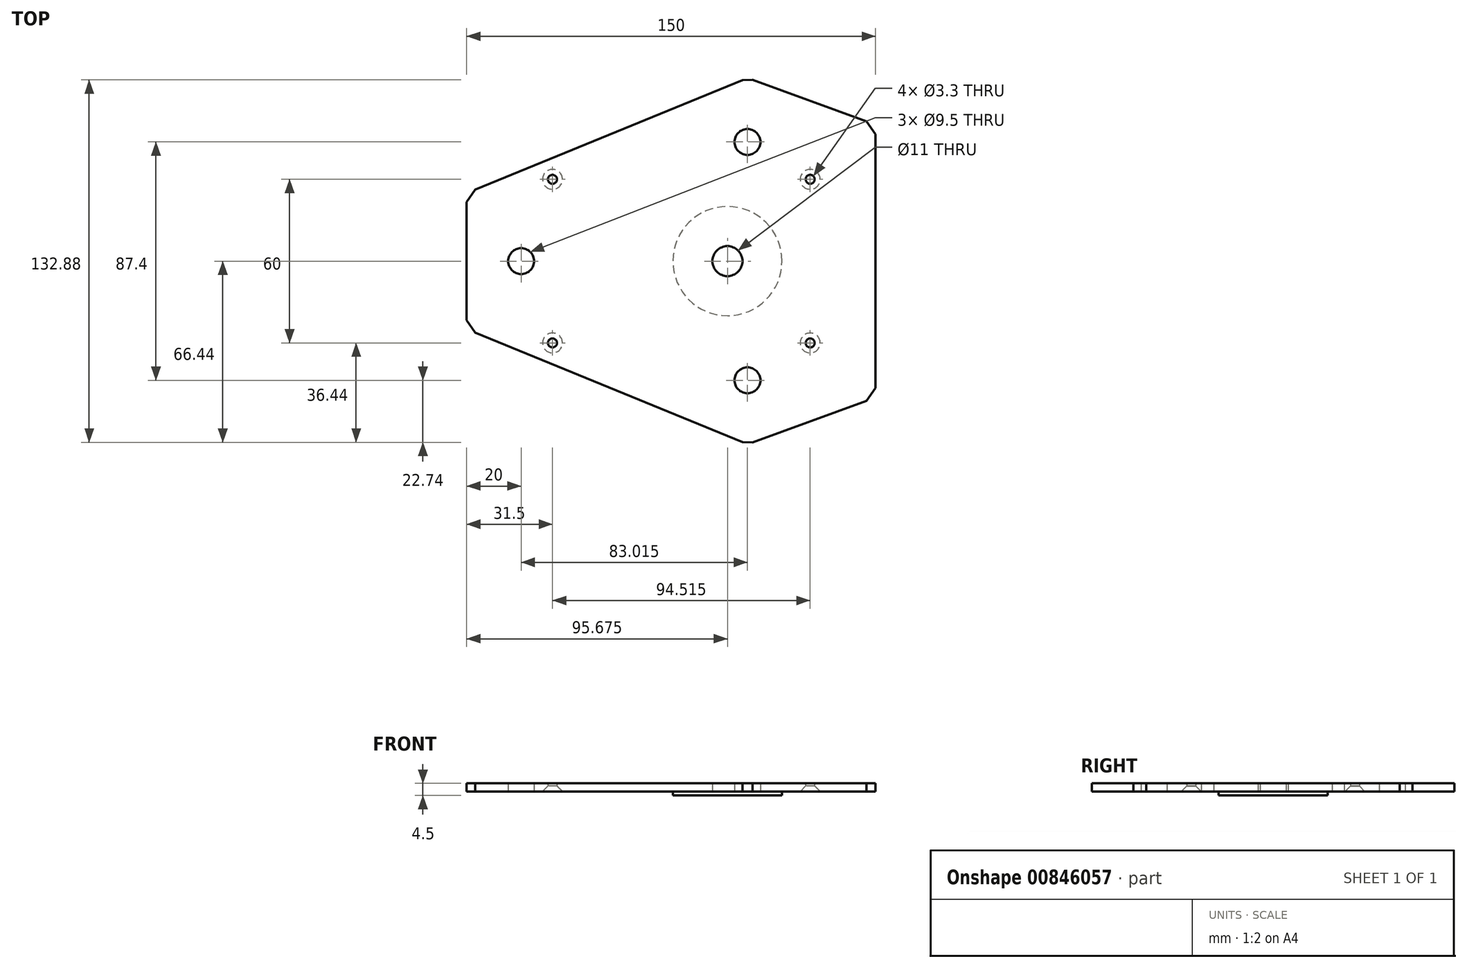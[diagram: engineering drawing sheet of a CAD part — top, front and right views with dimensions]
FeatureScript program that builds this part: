
annotation { "Feature Type Name" : "Feature", "Feature Type Description" : "" }
export const myFeature = defineFeature(function(context is Context, id is Id, definition is map)
    precondition{}
    {
        {
            var Q0;
            Q0=qCreatedBy(makeId("Top.planeOp"),FACE);
            var sketch = newSketch(context, id + "F0", { "sketchPlane" : qUnion([Q0])});
            skLineSegment(sketch, "E0", {"start": v(74.5, 0) * mm, "end": v(74.5, -50) * mm});
            skLineSegment(sketch, "E1", {"start": v(74.5, 0) * mm, "end": v(74.5, 50) * mm});
            skLineSegment(sketch, "E2", {"start": v(74.5, 50) * mm, "end": v(27.52, 67.1) * mm});
            skLineSegment(sketch, "E3", {"start": v(-75.5, 0) * mm, "end": v(-75.5, 25) * mm});
            skLineSegment(sketch, "E4", {"start": v(-75.5, 0) * mm, "end": v(-75.5, -25) * mm});
            skLineSegment(sketch, "E5", {"start": v(-75.5, 25) * mm, "end": v(27.52, 67.1) * mm});
            skLineSegment(sketch, "E6", {"start": v(-75.5, 0) * mm, "end": v(74.5, 0) * mm});
            skLineSegment(sketch, "E7.MirrorCS", {"start": v(74.5, -50) * mm, "end": v(27.52, -67.1) * mm});
            skLineSegment(sketch, "E8", {"start": v(-75.5, -25) * mm, "end": v(27.52, -67.1) * mm});
            skLineSegment(sketch, "E9.bottom", {"start": v(-32.18, 14.6) * mm, "end": v(-21.68, 14.6) * mm});
            skLineSegment(sketch, "E9.top", {"start": v(-32.18, -14.6) * mm, "end": v(-21.68, -14.6) * mm});
            skLineSegment(sketch, "E9.right", {"start": v(31.17, 14.6) * mm, "end": v(31.17, 1.3) * mm});
            skLineSegment(sketch, "E10", {"start": v(-21.68, 14.6) * mm, "end": v(-21.68, 16.53) * mm});
            skLineSegment(sketch, "E11", {"start": v(-13.48, 14.6) * mm, "end": v(-13.48, 16.53) * mm});
            skArc(sketch, "E12", {"start": v(-13.48, 16.53) * mm, "mid": v(-17.58, 20.63) * mm, "end": v(-21.68, 16.53) * mm});
            skLineSegment(sketch, "E13.trimOffspring", {"start": v(-13.48, 14.6) * mm, "end": v(12.48, 14.6) * mm});
            skArc(sketch, "E14.MirrorCS", {"start": v(12.48, 16.53) * mm, "mid": v(16.58, 20.63) * mm, "end": v(20.68, 16.53) * mm});
            skLineSegment(sketch, "E15.MirrorCS", {"start": v(20.68, 14.6) * mm, "end": v(20.68, 16.53) * mm});
            skLineSegment(sketch, "E16.MirrorCS", {"start": v(12.48, 14.6) * mm, "end": v(12.48, 16.53) * mm});
            skLineSegment(sketch, "E17.MirrorCS", {"start": v(-21.68, -14.6) * mm, "end": v(-21.68, -16.53) * mm});
            skArc(sketch, "E18.MirrorCS", {"start": v(-13.48, -16.53) * mm, "mid": v(-17.58, -20.63) * mm, "end": v(-21.68, -16.53) * mm});
            skLineSegment(sketch, "E19.MirrorCS", {"start": v(-13.48, -14.6) * mm, "end": v(-13.48, -16.53) * mm});
            skLineSegment(sketch, "E20.MirrorCS", {"start": v(12.47, -14.6) * mm, "end": v(12.48, -16.53) * mm});
            skArc(sketch, "E21.MirrorCS", {"start": v(12.47, -16.53) * mm, "mid": v(16.57, -20.63) * mm, "end": v(20.67, -16.53) * mm});
            skLineSegment(sketch, "E22.MirrorCS", {"start": v(20.67, -14.6) * mm, "end": v(20.67, -16.53) * mm});
            skLineSegment(sketch, "E23.trimOffspring", {"start": v(-13.48, -14.6) * mm, "end": v(12.47, -14.6) * mm});
            skLineSegment(sketch, "E24.trimOffspring", {"start": v(20.67, -14.6) * mm, "end": v(31.17, -14.6) * mm});
            skLineSegment(sketch, "E25.trimOffspring", {"start": v(20.68, 14.6) * mm, "end": v(31.17, 14.6) * mm});
            skPoint(sketch, "E26.end.orphan", {"position": v(31.17, 0) * mm});
            skPoint(sketch, "E26.start.orphan", {"position": v(-32.18, 0) * mm});
            skLineSegment(sketch, "E27.trimOffspring", {"start": v(-32.18, -1.3) * mm, "end": v(-32.18, -14.6) * mm});
            skLineSegment(sketch, "E28", {"start": v(-32.18, 1.3) * mm, "end": v(-32.18, 14.6) * mm});
            skLineSegment(sketch, "E29.MirrorCS", {"start": v(31.17, 1.3) * mm, "end": v(38.76, 1.3) * mm});
            skLineSegment(sketch, "E30.MirrorCS", {"start": v(38.76, 1.3) * mm, "end": v(38.76, -1.3) * mm});
            skLineSegment(sketch, "E31.MirrorCS", {"start": v(31.17, -1.3) * mm, "end": v(38.76, -1.3) * mm});
            skLineSegment(sketch, "E32", {"start": v(-32.17, 1.3) * mm, "end": v(-32.17, -1.3) * mm});
            skLineSegment(sketch, "E33.trimOffspring", {"start": v(31.17, -1.3) * mm, "end": v(31.17, -14.6) * mm});
            skCircle(sketch, "E34", {"center": v(-55.5, 0) * mm, "radius": 4.75 * mm});
            skCircle(sketch, "E35", {"center": v(-44, 30) * mm, "radius": 1.65 * mm});
            skCircle(sketch, "E36.MirrorC", {"center": v(-44, -30) * mm, "radius": 1.65 * mm});
            skCircle(sketch, "E37", {"center": v(27.52, 43.7) * mm, "radius": 4.75 * mm});
            skCircle(sketch, "E38.MirrorC", {"center": v(27.52, -43.7) * mm, "radius": 4.75 * mm});
            skCircle(sketch, "E39", {"center": v(50.52, 30) * mm, "radius": 1.65 * mm});
            skCircle(sketch, "E40.MirrorC", {"center": v(50.52, -30) * mm, "radius": 1.65 * mm});
            skCircle(sketch, "E41", {"center": v(20.18, 0) * mm, "radius": 5.5 * mm});
            skSolve(sketch);
        }
        {
            var Q0;
            {var subQ8=sQuery(id+"F0.wireOp",EDGE,"E1");Q0=makeQuery(id+"F0.imprint","IMPRINT",FACE,{"disambiguationData":[TD([[makeQuery(id+"F0.imprint","IMPRINT",EDGE,{"derivedFrom":subQ8}),1.0]])]});}
            var Q1;
            {var subQ11=sQuery(id+"F0.wireOp",EDGE,"E0");Q1=makeQuery(id+"F0.imprint","IMPRINT",FACE,{"disambiguationData":[TD([[makeQuery(id+"F0.imprint","IMPRINT",EDGE,{"derivedFrom":subQ11}),-1.0]])]});}
            var Q2;
            Q2=makeQuery(id+"F0.imprint","IMPRINT",FACE,{"disambiguationData":[TD([[makeQuery(id+"F0.imprint","IMPRINT",EDGE,{"derivedFrom":sQuery(id+"F0.wireOp",EDGE,"E9.top")}),1.0]])]});
            var Q3;
            Q3=makeQuery(id+"F0.imprint","IMPRINT",FACE,{"disambiguationData":[TD([[makeQuery(id+"F0.imprint","IMPRINT",EDGE,{"derivedFrom":sQuery(id+"F0.wireOp",EDGE,"E9.bottom")}),-1.0]])]});
            extrude(context, id + "F1", {"entities" : qUnion([Q0, Q1, Q2, Q3]), "depth" : 3 * mm, "offsetDistance" : 25 * mm});
        }
        {
            var Q0;
            Q0=makeQuery(id+"F1.opExtrude","CAP_EDGE",EDGE,{"disambiguationData":[OSD([sQuery(id+"F0.wireOp",EDGE,"E36.MirrorC")])],"isStart":true});
            var Q1;
            Q1=makeQuery(id+"F1.opExtrude","CAP_EDGE",EDGE,{"disambiguationData":[OSD([sQuery(id+"F0.wireOp",EDGE,"E35")])],"isStart":true});
            var Q2;
            Q2=makeQuery(id+"F1.opExtrude","CAP_EDGE",EDGE,{"disambiguationData":[OSD([sQuery(id+"F0.wireOp",EDGE,"E39")])],"isStart":true});
            var Q3;
            Q3=makeQuery(id+"F1.opExtrude","CAP_EDGE",EDGE,{"disambiguationData":[OSD([sQuery(id+"F0.wireOp",EDGE,"E40.MirrorC")])],"isStart":true});
            chamfer(context, id + "F2", {"entities" : qUnion([Q0, Q1, Q2, Q3]), "width" : 2 * mm, "tangentPropagation" : true});
        }
        {
            var Q0;
            Q0=makeQuery(id+"F1.opExtrude","CAP_FACE",FACE,{"disambiguationData":[OSD([sQuery(id+"F0.wireOp",EDGE,"E0"),sQuery(id+"F0.wireOp",EDGE,"E1"),sQuery(id+"F0.wireOp",EDGE,"E2"),sQuery(id+"F0.wireOp",EDGE,"E3"),sQuery(id+"F0.wireOp",EDGE,"E4"),sQuery(id+"F0.wireOp",EDGE,"E5"),sQuery(id+"F0.wireOp",EDGE,"E7.MirrorCS"),sQuery(id+"F0.wireOp",EDGE,"E8"),sQuery(id+"F0.wireOp",EDGE,"E34"),sQuery(id+"F0.wireOp",EDGE,"E35"),sQuery(id+"F0.wireOp",EDGE,"E36.MirrorC"),sQuery(id+"F0.wireOp",EDGE,"E37"),sQuery(id+"F0.wireOp",EDGE,"E38.MirrorC"),sQuery(id+"F0.wireOp",EDGE,"E39"),sQuery(id+"F0.wireOp",EDGE,"E40.MirrorC"),sQuery(id+"F0.wireOp",EDGE,"E41")])],"isStart":true});
            var sketch = newSketch(context, id + "F3", { "sketchPlane" : qUnion([Q0])});
            skCircle(sketch, "E42", {"center": v(20.18, 0) * mm, "radius": 20 * mm});
            skCircle(sketch, "E43", {"center": v(20.18, 0) * mm, "radius": 5.5 * mm});
            skSolve(sketch);
        }
        {
            var Q0;
            Q0=makeQuery(id+"F3.imprint","IMPRINT",FACE,{"disambiguationData":[TD([[makeQuery(id+"F3.imprint","IMPRINT",EDGE,{"derivedFrom":sQuery(id+"F3.wireOp",EDGE,"E42")}),1.0]])]});
            extrude(context, id + "F4", {"entities" : qUnion([Q0]), "operationType" : NewBodyOperationType.ADD, "depth" : 1.5 * mm, "offsetDistance" : 25 * mm});
        }
        {
            var Q0;
            Q0=makeQuery(id+"F1.opExtrude","SWEPT_EDGE",EDGE,{"disambiguationData":[OSD([sQuery(id+"F0.wireOp",EDGE,"E4"),sQuery(id+"F0.wireOp",EDGE,"E8")])]});
            var Q1;
            Q1=makeQuery(id+"F1.opExtrude","SWEPT_EDGE",EDGE,{"disambiguationData":[OSD([sQuery(id+"F0.wireOp",EDGE,"E7.MirrorCS"),sQuery(id+"F0.wireOp",EDGE,"E8")])]});
            var Q2;
            Q2=makeQuery(id+"F1.opExtrude","SWEPT_EDGE",EDGE,{"disambiguationData":[OSD([sQuery(id+"F0.wireOp",EDGE,"E0"),sQuery(id+"F0.wireOp",EDGE,"E7.MirrorCS")])]});
            var Q3;
            Q3=makeQuery(id+"F1.opExtrude","SWEPT_EDGE",EDGE,{"disambiguationData":[OSD([sQuery(id+"F0.wireOp",EDGE,"E1"),sQuery(id+"F0.wireOp",EDGE,"E2")])]});
            var Q4;
            Q4=makeQuery(id+"F1.opExtrude","SWEPT_EDGE",EDGE,{"disambiguationData":[OSD([sQuery(id+"F0.wireOp",EDGE,"E2"),sQuery(id+"F0.wireOp",EDGE,"E5")])]});
            var Q5;
            Q5=makeQuery(id+"F1.opExtrude","SWEPT_EDGE",EDGE,{"disambiguationData":[OSD([sQuery(id+"F0.wireOp",EDGE,"E3"),sQuery(id+"F0.wireOp",EDGE,"E5")])]});
            chamfer(context, id + "F5", {"entities" : qUnion([Q0, Q1, Q2, Q3, Q4, Q5]), "width" : 5 * mm, "tangentPropagation" : true});
        }
    });
